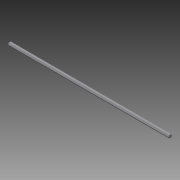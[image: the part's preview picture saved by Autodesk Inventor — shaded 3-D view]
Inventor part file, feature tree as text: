
AUTODESK INVENTOR PART (.ipt)
format: ipt  version: 2015 SP1 (Build 190203100, 203)  size: 78,336 bytes
history: native  units: in
note: dims shown in document units (in); Inventor stores cm internally (conversion verified against a paired STEP export)
features: extrude x1, sketch x1
ambient origin geometry x8: Origin, YZ Plane, XZ Plane, XY Plane, X Axis, Y Axis, Z Axis, Center Point
bodies: Solid1 (feature_tree)
feature tree (2):
  extrude  "Extrusion1"  Depth=0.5in
  sketch  "Sketch1"  dims[d0=0.5in d1=0.5in d2=0.5in d3=0.25in d4=120.0deg d5=120.0deg d6=0.25in d7=0.25in d8=27.0in d9=0.0in]
